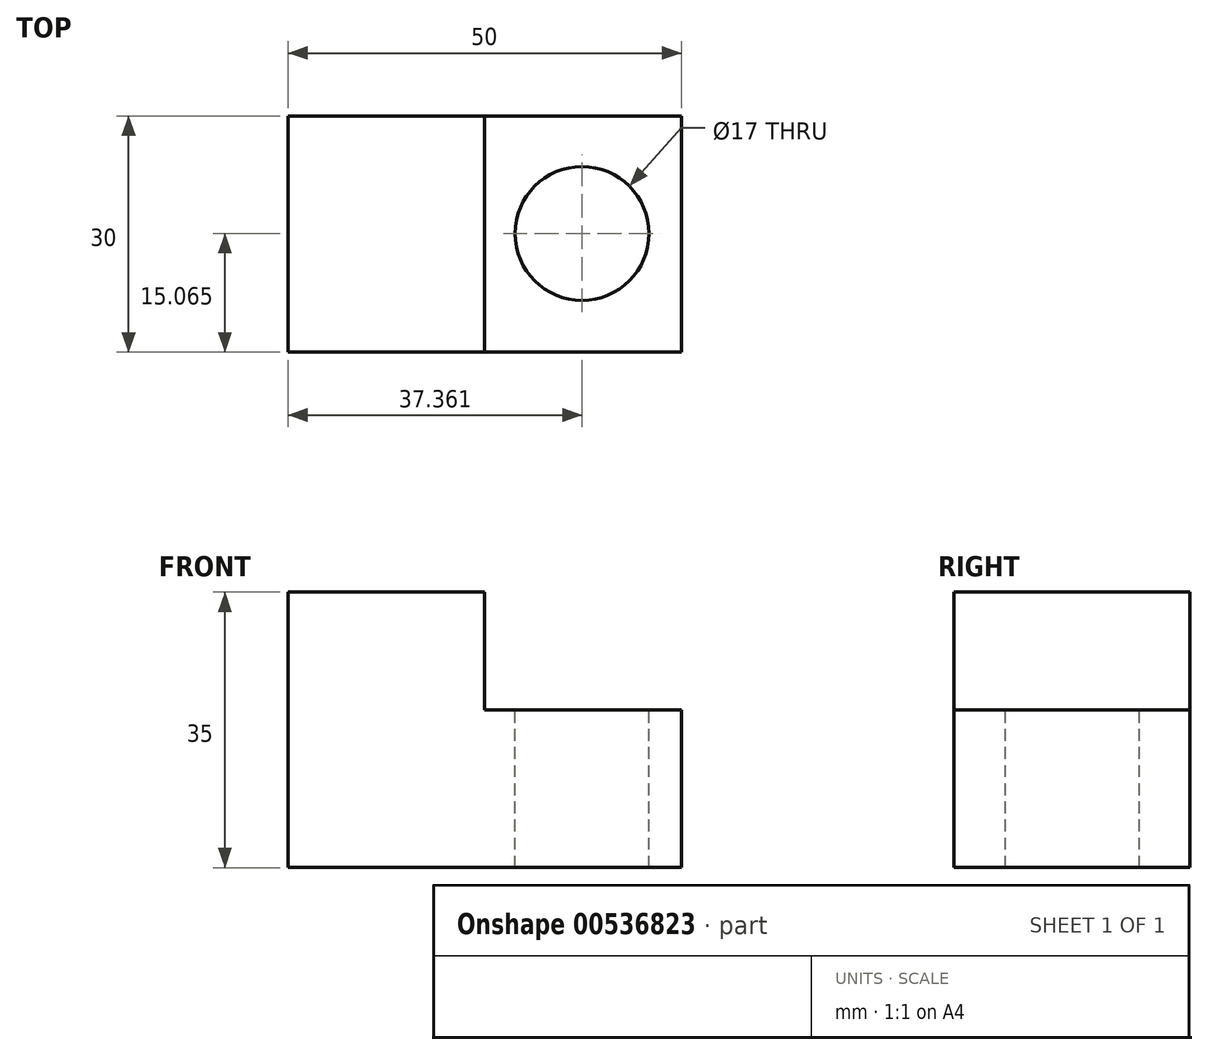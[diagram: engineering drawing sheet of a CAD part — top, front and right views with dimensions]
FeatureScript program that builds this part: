
annotation { "Feature Type Name" : "Feature", "Feature Type Description" : "" }
export const myFeature = defineFeature(function(context is Context, id is Id, definition is map)
    precondition{}
    {
        {
            var Q0;
            Q0=qCreatedBy(makeId("Front.planeOp"),FACE);
            var sketch = newSketch(context, id + "F0", { "sketchPlane" : qUnion([Q0])});
            skLineSegment(sketch, "E0", {"start": v(-31.93, -15.77) * mm, "end": v(18.07, -15.77) * mm});
            skLineSegment(sketch, "E1", {"start": v(18.07, -15.77) * mm, "end": v(18.07, 4.23) * mm});
            skLineSegment(sketch, "E2", {"start": v(18.07, 4.23) * mm, "end": v(-6.93, 4.23) * mm});
            skLineSegment(sketch, "E3", {"start": v(-6.93, 4.23) * mm, "end": v(-6.93, 19.23) * mm});
            skLineSegment(sketch, "E4", {"start": v(-6.93, 19.23) * mm, "end": v(-31.93, 19.23) * mm});
            skLineSegment(sketch, "E5", {"start": v(-31.93, 19.23) * mm, "end": v(-31.93, -15.77) * mm});
            skSolve(sketch);
        }
        {
            var Q0;
            Q0=makeQuery(id+"F0.imprint","IMPRINT",FACE,{"disambiguationData":[TD([[makeQuery(id+"F0.imprint","IMPRINT",EDGE,{"derivedFrom":sQuery(id+"F0.wireOp",EDGE,"E0")}),1.0]])]});
            extrude(context, id + "F1", {"entities" : qUnion([Q0]), "depth" : 30 * mm, "offsetDistance" : 25 * mm});
        }
        {
            var Q0;
            Q0=makeQuery(id+"F1.opExtrude","SWEPT_FACE",FACE,{"disambiguationData":[OSD([sQuery(id+"F0.wireOp",EDGE,"E2")])]});
            var sketch = newSketch(context, id + "F2", { "sketchPlane" : qUnion([Q0])});
            skLineSegment(sketch, "E6", {"start": v(5.57, 0) * mm, "end": v(5.57, -15) * mm});
            skPoint(sketch, "E6.endSnap0", {"position": v(18.07, -15) * mm});
            skSolve(sketch);
        }
        {
            var Q0;
            {var subQ0=sQuery(id+"F0.wireOp",EDGE,"E2");Q0=makeQuery(id+"F2.imprint","IMPRINT",FACE,{"disambiguationData":[TD([[makeQuery(id+"F2.imprint","IMPRINT",EDGE,{"derivedFrom":makeQuery(id+"F1.opExtrude","CAP_EDGE",EDGE,{"disambiguationData":[OSD([subQ0])],"isStart":false})}),-1.0]])]});}
            var sketch = newSketch(context, id + "F3", { "sketchPlane" : qUnion([Q0])});
            skCircle(sketch, "E7", {"center": v(5.43, -14.94) * mm, "radius": 8.5 * mm});
            skSolve(sketch);
        }
        {
            var Q0;
            Q0=makeQuery(id+"F3.imprint","IMPRINT",FACE,{"disambiguationData":[TD([[makeQuery(id+"F3.imprint","IMPRINT",EDGE,{"derivedFrom":sQuery(id+"F3.wireOp",EDGE,"E7")}),1.0]])]});
            extrude(context, id + "F4", {"entities" : qUnion([Q0]), "operationType" : NewBodyOperationType.REMOVE, "endBound" : BoundingType.THROUGH_ALL, "oppositeDirection" : true, "depth" : 20 * mm, "offsetDistance" : 25 * mm});
        }
    });
